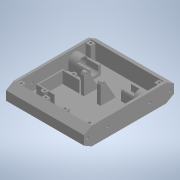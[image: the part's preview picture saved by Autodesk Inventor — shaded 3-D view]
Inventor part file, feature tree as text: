
AUTODESK INVENTOR PART (.ipt)
format: ipt  version: 2020 (Build 240168000, 168)  size: 514,048 bytes
history: native  units: in
note: dims shown in document units (in); Inventor stores cm internally (conversion verified against a paired STEP export)
features: sketch x15, projected_geometry x15, extrude x14, mirror x4, plane x2
ambient origin geometry x8: Origin, YZ Plane, XZ Plane, XY Plane, X Axis, Y Axis, Z Axis, Center Point
bodies: Solid1 (feature_tree)
feature tree (50):
  extrude  "Extrusion1"  Depth=5.9055in
  extrude  "Extrusion2"  TaperAngle=0.0deg  [1 undecoded]
  extrude  "Extrusion3"  Depth=1.063in
  extrude  "Extrusion4"  Depth=0.315in
  extrude  "Extrusion5"  TaperAngle=0.0deg  [1 undecoded]
  extrude  "Extrusion6"  Depth=0.5906in
  mirror  "Mirror1"
  extrude  "Extrusion7"  Depth=0.0787in
  mirror  "Mirror2"
  extrude  "Extrusion8"  Depth=0.6102in
  mirror  "Mirror3"
  plane  "Work Plane1"
  extrude  "Extrusion9"  Depth=0.7874in TaperAngle=0.0deg
  mirror  "Mirror4"
  extrude  "Extrusion10"  Depth=6.063in TaperAngle=0.0deg
  extrude  "Extrusion11"  Depth=0.1575in
  extrude  "Extrusion12"  TaperAngle=0.0deg  [1 undecoded]
  extrude  "Extrusion13"  Depth=0.2756in
  extrude  "Extrusion14"  Depth=0.4331in
  plane  "Work Plane2"
  sketch  "Sketch18"  dims[d34=0.122in d38=2.7559in d40=0.061in d41=0.0909in d42=0.2362in d43=0.0in d44=60.0deg d45=0.0787in d46=0.315in d48=0.993in d49=0.0in d51=0.1575in d52=0.1575in d53=0.2756in d54=0.0in d55=0.4724in d56=1.1614in d57=1.5748in d58=1.5945in d59=0.0787in d60=0.0787in d62=0.315in d63=0.7677in d64=0.0in d65=0.1575in d66=0.1575in d67=0.2756in d68=0.0in d69=0.8268in d70=0.2953in d71=0.0394in d72=0.0in d76=0.1575in d77=120.0deg d79=0.1969in d80=0.1969in d81=0.1969in d82=0.1969in d83=0.1969in d85=120.0deg]
  sketch  "Sketch1"  dims[d0=1.1811in d1=5.9055in]
  sketch  "Sketch2"  dims[d2=5.1181in d3=0.0in]
  projected_geometry  "Projected Loop1"
  sketch  "Sketch3"  dims[d4=0.1575in d5=1.063in]
  projected_geometry  "Projected Loop2"
  projected_geometry  "Projected Loop3"
  sketch  "Sketch4"  dims[d6=0.0in d8=0.315in]
  sketch  "Sketch5"  dims[d10=0.993in d11=0.0in]
  projected_geometry  "Projected Loop4"
  sketch  "Sketch6"  dims[d12=0.6496in d13=0.5906in]
  sketch  "Sketch7"  dims[d14=1.5748in d15=0.0787in]
  sketch  "Sketch9"  dims[d16=0.5512in d17=0.0in d18=0.6102in]
  sketch  "Sketch10"  dims[d19=0.4803in d20=0.7874in d21=0.0in]
  sketch  "Sketch12"  dims[d22=0.1654in d23=6.063in d24=0.0in]
  projected_geometry  "Projected Loop6"
  projected_geometry  "Projected Loop7"
  projected_geometry  "Projected Loop8"
  sketch  "Sketch13"  dims[d25=0.5114in d26=0.1575in]
  projected_geometry  "Projected Loop9"
  projected_geometry  "Projected Loop10"
  projected_geometry  "Projected Loop11"
  projected_geometry  "Projected Loop12"
  projected_geometry  "Projected Loop13"
  projected_geometry  "Projected Loop14"
  sketch  "Sketch14"  dims[d27=1.5748in d28=0.0in d29=0.0in]
  sketch  "Sketch15"  dims[d30=0.1575in d31=0.2756in]
  projected_geometry  "Projected Loop15"
  sketch  "Sketch16"  dims[d32=0.0in d33=0.4331in]
  projected_geometry  "Projected Loop18"
note: 3 required parameter values undecoded (feature->parameter linkage not recoverable at this tier; creation-order binding heuristic only, values carry confidence <= 0.55)
